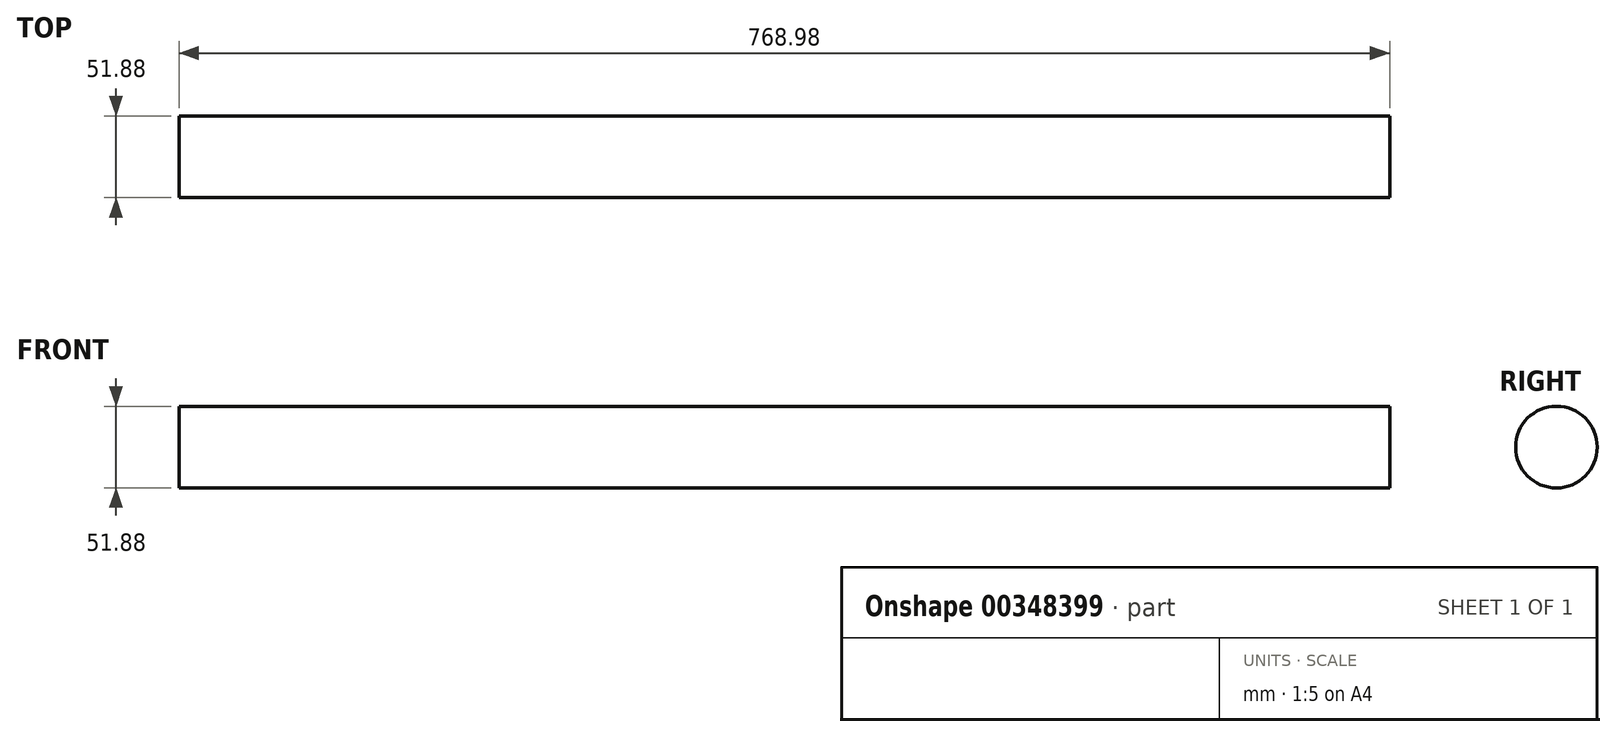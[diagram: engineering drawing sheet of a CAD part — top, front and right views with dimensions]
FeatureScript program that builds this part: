
annotation { "Feature Type Name" : "Feature", "Feature Type Description" : "" }
export const myFeature = defineFeature(function(context is Context, id is Id, definition is map)
    precondition{}
    {
        {
            var Q0;
            Q0=qCreatedBy(makeId("Right.planeOp"),FACE);
            var sketch = newSketch(context, id + "F0", { "sketchPlane" : qUnion([Q0])});
            skCircle(sketch, "E0", {"center": v(0, 0) * mm, "radius": 25.94 * mm});
            skSolve(sketch);
        }
        {
            var Q0;
            Q0=qCreatedBy(makeId("Front.planeOp"),FACE);
            var sketch = newSketch(context, id + "F1", { "sketchPlane" : qUnion([Q0])});
            skLineSegment(sketch, "E1", {"start": v(0, 0) * mm, "end": v(-768.98, 0) * mm});
            skSolve(sketch);
        }
        {
            var Q0;
            Q0=makeQuery(id+"F0.imprint","IMPRINT",FACE,{"disambiguationData":[TD([[makeQuery(id+"F0.imprint","IMPRINT",EDGE,{"derivedFrom":sQuery(id+"F0.wireOp",EDGE,"E0")}),1.0]])]});
            var Q1;
            Q1=sQuery(id+"F1.wireOp",EDGE,"E1");
            sweep(context, id + "F2", {"profiles" : qUnion([Q0]), "path" : qUnion([Q1])});
        }
    });
